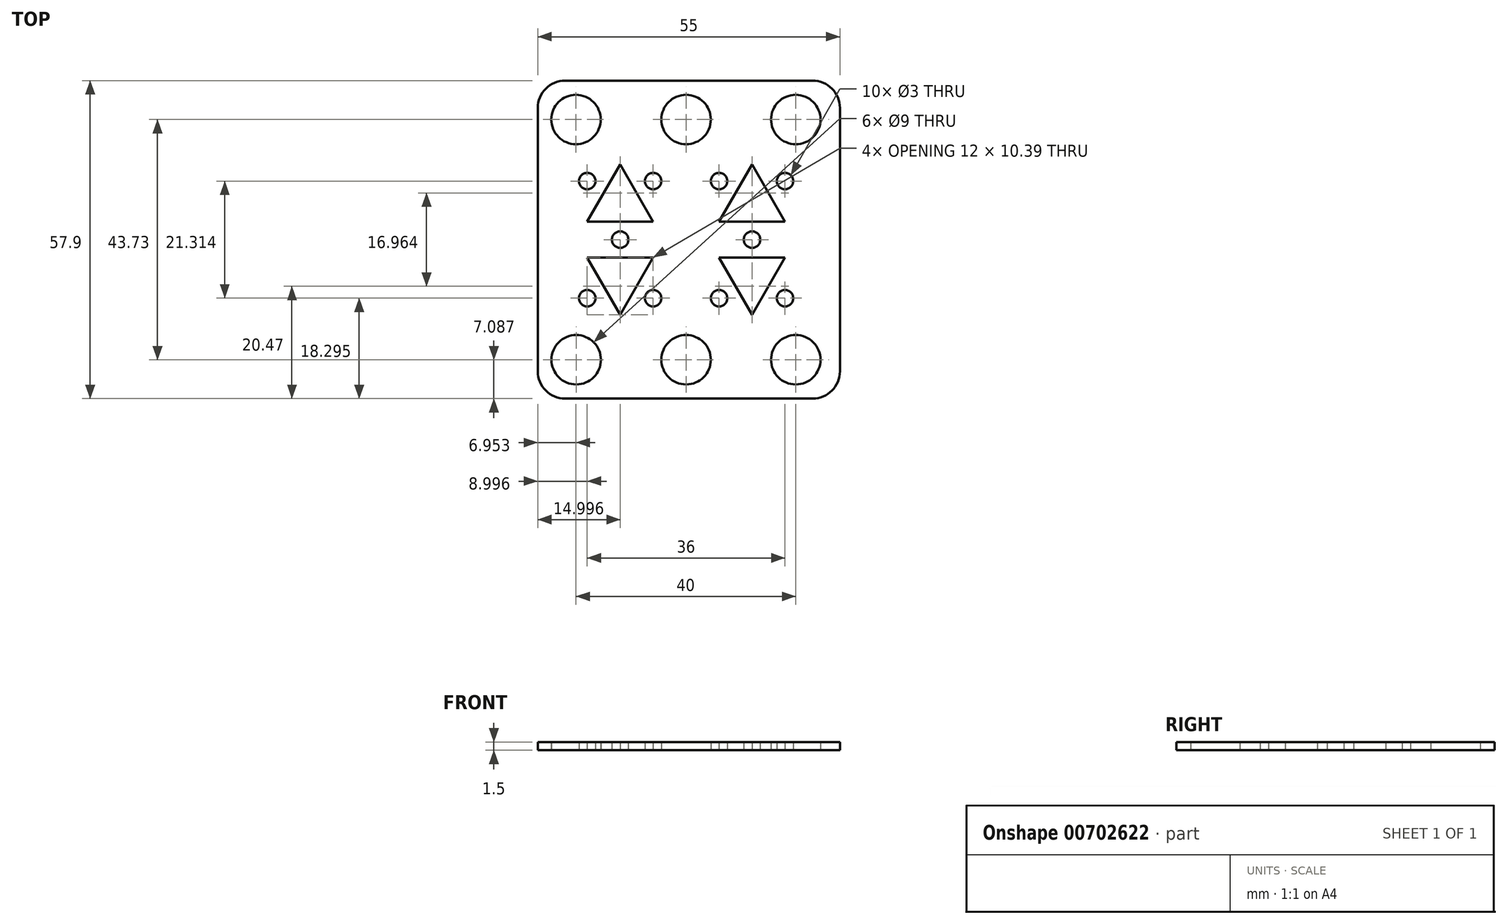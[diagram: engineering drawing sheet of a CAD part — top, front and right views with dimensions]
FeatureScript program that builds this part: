
annotation { "Feature Type Name" : "Feature", "Feature Type Description" : "" }
export const myFeature = defineFeature(function(context is Context, id is Id, definition is map)
    precondition{}
    {
        {
            var Q0;
            Q0=qCreatedBy(makeId("Top.planeOp"),FACE);
            var sketch = newSketch(context, id + "F0", { "sketchPlane" : qUnion([Q0])});
            skPoint(sketch, "E0.middle", {"position": v(0.82, -0.23) * mm});
            skCircle(sketch, "E1", {"center": v(-19.68, -22.1) * mm, "radius": 4.5 * mm});
            skCircle(sketch, "E2.MirrorC", {"center": v(20.27, -22.1) * mm, "radius": 4.5 * mm});
            skCircle(sketch, "E3.MirrorC", {"center": v(-19.73, 21.64) * mm, "radius": 4.5 * mm});
            skCircle(sketch, "E4.MirrorC", {"center": v(20.27, 21.64) * mm, "radius": 4.5 * mm});
            skCircle(sketch, "E5", {"center": v(0.32, -22.1) * mm, "radius": 4.5 * mm});
            skLineSegment(sketch, "E6", {"start": v(20.27, 21.64) * mm, "end": v(20.27, -22.1) * mm, "construction": true});
            skCircle(sketch, "E7.MirrorC", {"center": v(0.32, 21.64) * mm, "radius": 4.5 * mm});
            skLineSegment(sketch, "E8.MirrorCS", {"start": v(-17.68, -3.51) * mm, "end": v(-5.68, -3.51) * mm});
            skLineSegment(sketch, "E9.MirrorCS", {"start": v(-5.68, -3.51) * mm, "end": v(-11.68, -13.9) * mm});
            skLineSegment(sketch, "E10.MirrorCS", {"start": v(-11.68, -13.9) * mm, "end": v(-17.68, -3.51) * mm});
            skLineSegment(sketch, "E11.bottom", {"start": v(-26.68, -29.18) * mm, "end": v(28.32, -29.18) * mm});
            skLineSegment(sketch, "E11.top", {"start": v(-26.68, 28.72) * mm, "end": v(28.32, 28.72) * mm});
            skLineSegment(sketch, "E11.left", {"start": v(-26.68, -29.18) * mm, "end": v(-26.68, 28.72) * mm});
            skLineSegment(sketch, "E11.right", {"start": v(28.32, -29.18) * mm, "end": v(28.32, 28.72) * mm});
            skLineSegment(sketch, "E12", {"start": v(0.32, 21.64) * mm, "end": v(0.32, -22.1) * mm, "construction": true});
            skCircle(sketch, "E13", {"center": v(-5.68, -10.88) * mm, "radius": 1.5 * mm});
            skLineSegment(sketch, "E14.MirrorCS", {"start": v(6.32, -3.51) * mm, "end": v(12.32, -13.9) * mm});
            skLineSegment(sketch, "E15.MirrorCS", {"start": v(18.32, -3.51) * mm, "end": v(6.32, -3.51) * mm});
            skLineSegment(sketch, "E16.MirrorCS", {"start": v(12.32, -13.9) * mm, "end": v(18.32, -3.51) * mm});
            skCircle(sketch, "E17.MirrorC", {"center": v(6.32, -10.88) * mm, "radius": 1.5 * mm});
            skCircle(sketch, "E18", {"center": v(-17.68, -10.88) * mm, "radius": 1.5 * mm});
            skCircle(sketch, "E19.MirrorC", {"center": v(18.32, -10.88) * mm, "radius": 1.5 * mm});
            skLineSegment(sketch, "E20", {"start": v(0.82, -0.23) * mm, "end": v(-21.65, -0.23) * mm, "construction": true});
            skLineSegment(sketch, "E21.MirrorCS", {"start": v(-17.68, 3.06) * mm, "end": v(-5.68, 3.06) * mm});
            skLineSegment(sketch, "E22.MirrorCS", {"start": v(-5.68, 3.06) * mm, "end": v(-11.68, 13.45) * mm});
            skLineSegment(sketch, "E23.MirrorCS", {"start": v(-11.68, 13.45) * mm, "end": v(-17.68, 3.06) * mm});
            skCircle(sketch, "E24.MirrorC", {"center": v(-17.68, 10.43) * mm, "radius": 1.5 * mm});
            skCircle(sketch, "E25.MirrorC", {"center": v(-5.68, 10.43) * mm, "radius": 1.5 * mm});
            skCircle(sketch, "E26.MirrorC", {"center": v(6.32, 10.43) * mm, "radius": 1.5 * mm});
            skLineSegment(sketch, "E27.MirrorCS", {"start": v(6.32, 3.06) * mm, "end": v(12.32, 13.45) * mm});
            skLineSegment(sketch, "E28.MirrorCS", {"start": v(12.32, 13.45) * mm, "end": v(18.32, 3.06) * mm});
            skCircle(sketch, "E29.MirrorC", {"center": v(18.32, 10.43) * mm, "radius": 1.5 * mm});
            skLineSegment(sketch, "E30.MirrorCS", {"start": v(18.32, 3.06) * mm, "end": v(6.32, 3.06) * mm});
            skCircle(sketch, "E31", {"center": v(12.32, -0.23) * mm, "radius": 1.5 * mm});
            skPoint(sketch, "E31.centerSnap0", {"position": v(12.32, -3.51) * mm});
            skCircle(sketch, "E32.MirrorC", {"center": v(-11.68, -0.23) * mm, "radius": 1.5 * mm});
            skSolve(sketch);
        }
        {
            var Q0;
            Q0=makeQuery(id+"F0.imprint","IMPRINT",FACE,{"disambiguationData":[TD([[makeQuery(id+"F0.imprint","IMPRINT",EDGE,{"derivedFrom":sQuery(id+"F0.wireOp",EDGE,"E1")}),-1.0]])]});
            extrude(context, id + "F1", {"entities" : qUnion([Q0]), "depth" : 1.5 * mm, "offsetDistance" : 25 * mm});
        }
        {
            var Q0;
            Q0=makeQuery(id+"F1.opExtrude","SWEPT_EDGE",EDGE,{"disambiguationData":[OSD([sQuery(id+"F0.wireOp",EDGE,"E11.top"),sQuery(id+"F0.wireOp",EDGE,"E11.left")])]});
            var Q1;
            Q1=makeQuery(id+"F1.opExtrude","SWEPT_EDGE",EDGE,{"disambiguationData":[OSD([sQuery(id+"F0.wireOp",EDGE,"E11.bottom"),sQuery(id+"F0.wireOp",EDGE,"E11.left")])]});
            var Q2;
            Q2=makeQuery(id+"F1.opExtrude","SWEPT_EDGE",EDGE,{"disambiguationData":[OSD([sQuery(id+"F0.wireOp",EDGE,"E11.bottom"),sQuery(id+"F0.wireOp",EDGE,"E11.right")])]});
            var Q3;
            Q3=makeQuery(id+"F1.opExtrude","SWEPT_EDGE",EDGE,{"disambiguationData":[OSD([sQuery(id+"F0.wireOp",EDGE,"E11.top"),sQuery(id+"F0.wireOp",EDGE,"E11.right")])]});
            fillet(context, id + "F2", {"entities" : qUnion([Q0, Q1, Q2, Q3]), "radius" : 5 * mm, "tangentPropagation" : true, "allowEdgeOverflow" : false});
        }
    });
